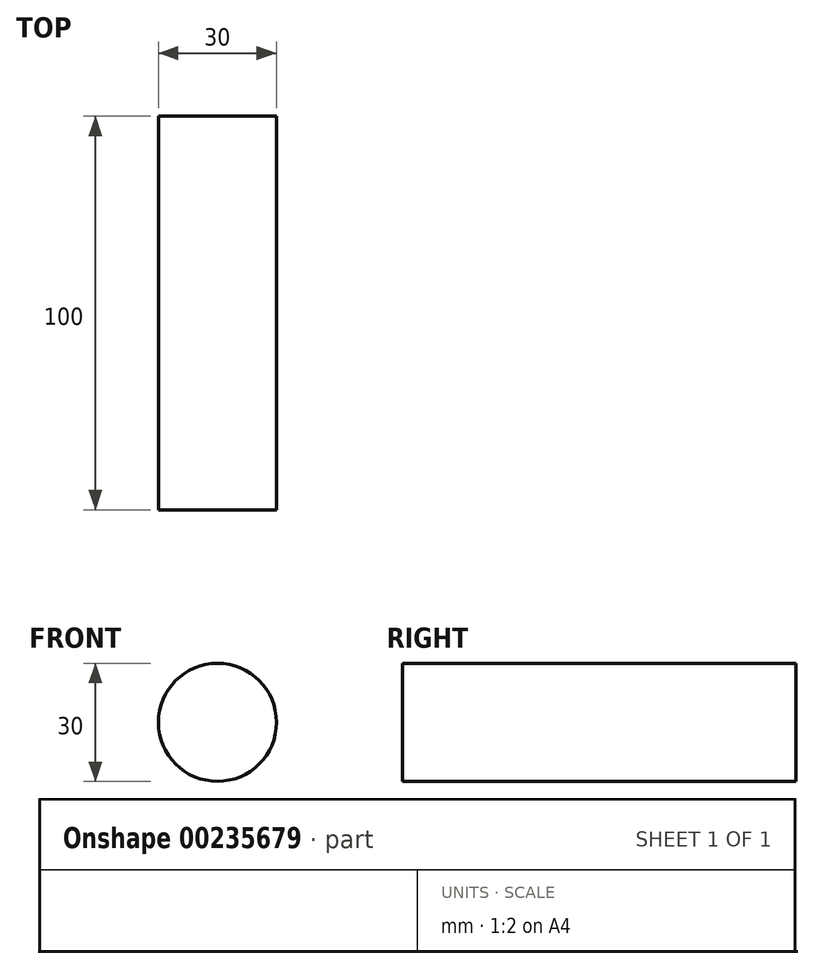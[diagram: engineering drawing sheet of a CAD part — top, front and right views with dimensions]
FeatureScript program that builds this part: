
annotation { "Feature Type Name" : "Feature", "Feature Type Description" : "" }
export const myFeature = defineFeature(function(context is Context, id is Id, definition is map)
    precondition{}
    {
        {
            var Q0;
            Q0=qCreatedBy(makeId("Front.planeOp"),FACE);
            var sketch = newSketch(context, id + "F0", { "sketchPlane" : qUnion([Q0])});
            skCircle(sketch, "E0", {"center": v(0, 0) * mm, "radius": 15 * mm});
            skSolve(sketch);
        }
        {
            var Q0;
            Q0 = qSketchRegion(id + "F0", true);
            extrude(context, id + "F1", {"entities" : qUnion([Q0]), "depth" : 100 * mm});
        }
    });
